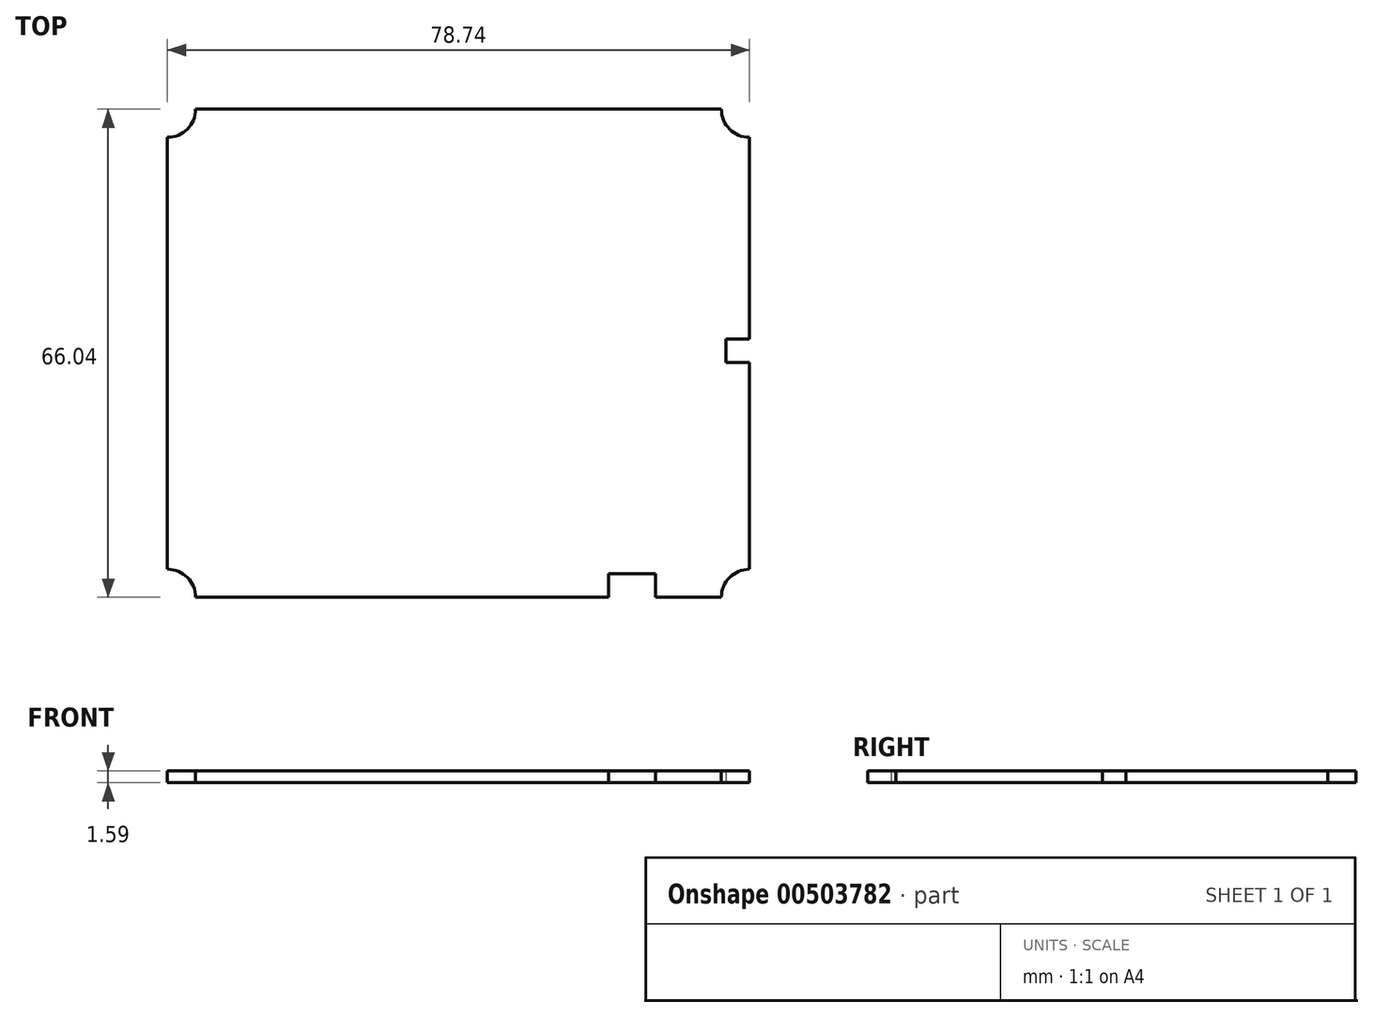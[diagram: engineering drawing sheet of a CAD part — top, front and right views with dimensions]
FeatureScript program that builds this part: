
annotation { "Feature Type Name" : "Feature", "Feature Type Description" : "" }
export const myFeature = defineFeature(function(context is Context, id is Id, definition is map)
    precondition{}
    {
        {
            var Q0;
            Q0=qCreatedBy(makeId("Top.planeOp"),FACE);
            var sketch = newSketch(context, id + "F0", { "sketchPlane" : qUnion([Q0])});
            skLineSegment(sketch, "E0.bottom", {"start": v(0, 0) * mm, "end": v(78.74, 0) * mm, "construction": true});
            skLineSegment(sketch, "E0.top", {"start": v(0, 66.04) * mm, "end": v(78.74, 66.04) * mm, "construction": true});
            skLineSegment(sketch, "E0.left", {"start": v(0, 0) * mm, "end": v(0, 66.04) * mm, "construction": true});
            skLineSegment(sketch, "E0.right", {"start": v(78.74, 0) * mm, "end": v(78.74, 66.04) * mm, "construction": true});
            skLineSegment(sketch, "E1.bottom", {"start": v(0, 0) * mm, "end": v(78.74, 0) * mm});
            skLineSegment(sketch, "E1.top", {"start": v(0, 66.04) * mm, "end": v(78.74, 66.04) * mm});
            skLineSegment(sketch, "E1.left", {"start": v(0, 0) * mm, "end": v(0, 66.04) * mm});
            skLineSegment(sketch, "E1.right", {"start": v(78.74, 0) * mm, "end": v(78.74, 66.04) * mm});
            skArc(sketch, "E2", {"start": v(0, 62.23) * mm, "mid": v(2.7, 63.35) * mm, "end": v(3.8, 66.04) * mm});
            skArc(sketch, "E3", {"start": v(74.93, 66.04) * mm, "mid": v(76.05, 63.35) * mm, "end": v(78.74, 62.23) * mm});
            skArc(sketch, "E4", {"start": v(78.74, 3.81) * mm, "mid": v(76.05, 2.7) * mm, "end": v(74.93, 0) * mm});
            skArc(sketch, "E5", {"start": v(0, 3.81) * mm, "mid": v(2.7, 2.7) * mm, "end": v(3.81, 0) * mm});
            skLineSegment(sketch, "E6", {"start": v(78.74, 0) * mm, "end": v(78.74, 31.75) * mm, "construction": true});
            skLineSegment(sketch, "E7.bottom", {"start": v(78.74, 31.75) * mm, "end": v(75.57, 31.75) * mm});
            skLineSegment(sketch, "E7.top", {"start": v(78.74, 34.92) * mm, "end": v(75.57, 34.92) * mm});
            skLineSegment(sketch, "E7.left", {"start": v(78.74, 31.75) * mm, "end": v(78.74, 34.92) * mm});
            skLineSegment(sketch, "E7.right", {"start": v(75.57, 31.75) * mm, "end": v(75.57, 34.92) * mm});
            skLineSegment(sketch, "E8", {"start": v(78.74, 0) * mm, "end": v(66.04, 0) * mm, "construction": true});
            skLineSegment(sketch, "E9.bottom", {"start": v(66.04, 0) * mm, "end": v(59.69, 0) * mm});
            skLineSegment(sketch, "E9.top", {"start": v(66.04, 3.18) * mm, "end": v(59.69, 3.17) * mm});
            skLineSegment(sketch, "E9.left", {"start": v(66.04, 0) * mm, "end": v(66.04, 3.18) * mm});
            skLineSegment(sketch, "E9.right", {"start": v(59.69, 0) * mm, "end": v(59.69, 3.17) * mm});
            skSolve(sketch);
        }
        {
            var Q0;
            {var subQ3=sQuery(id+"F0.wireOp",EDGE,"E2");Q0=makeQuery(id+"F0.imprint","IMPRINT",FACE,{"disambiguationData":[TD([[makeQuery(id+"F0.imprint","IMPRINT",EDGE,{"derivedFrom":subQ3}),-1.0]])]});}
            extrude(context, id + "F1", {"entities" : qUnion([Q0]), "depth" : 1.59 * mm});
        }
    });
